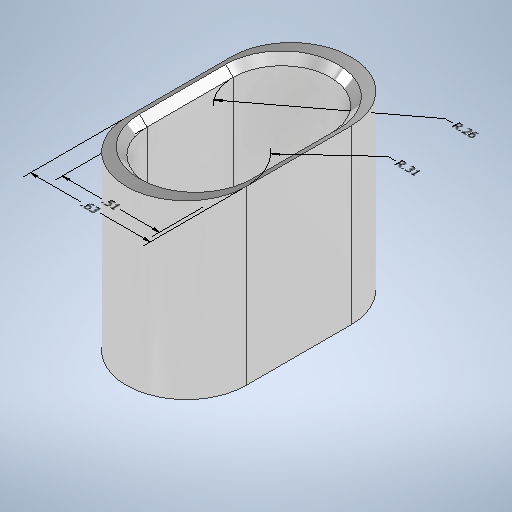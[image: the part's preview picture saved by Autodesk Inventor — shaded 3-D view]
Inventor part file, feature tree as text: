
AUTODESK INVENTOR PART (.ipt)
format: ipt  version: 2025.2 (Build 292293000, 293)  size: 273,408 bytes
history: native  units: in
note: dims shown in document units (in); Inventor stores cm internally (conversion verified against a paired STEP export)
features: other x5, extrude x3, sketch x3, chamfer x1
ambient origin geometry x8: Origin, YZ Plane, XZ Plane, XY Plane, X Axis, Y Axis, Z Axis, Center Point
bodies: Solid1 (feature_tree)
feature tree (12):
  other  "Annotations"
  extrude  "Extrusion1"  Depth=0.9055in TaperAngle=0.0deg
  extrude  "Extrusion2"  Depth=0.5118in
  extrude  "Extrusion3"  Depth=0.2559in
  chamfer  "Chamfer1"  Distance=0.0984in
  sketch  "Sketch1"  dims[d4=0.6299in d5=1.1811in d6=0.9055in d7=0.0in]
  sketch  "Sketch4"  dims[d11=0.9646in d12=0.5118in]
  sketch  "Sketch5"  dims[d13=0.7087in d14=0.0in d15=0.2559in d16=0.0984in d17=0.7087in d18=0.0in d19=0.0394in d20=0.0787in d21=45.0deg d25=0.9824in d26=0.2559in d27=0.1239in d28=0.2482in d29=0.6299in d32=0.1875in d33=0.1817in d34=0.5118in d35=1.1341in d36=0.315in]
  other  "Radial Dimension 1"
  other  "Linear Dimension 2"
  other  "Linear Dimension 3"
  other  "Radial Dimension 2"
